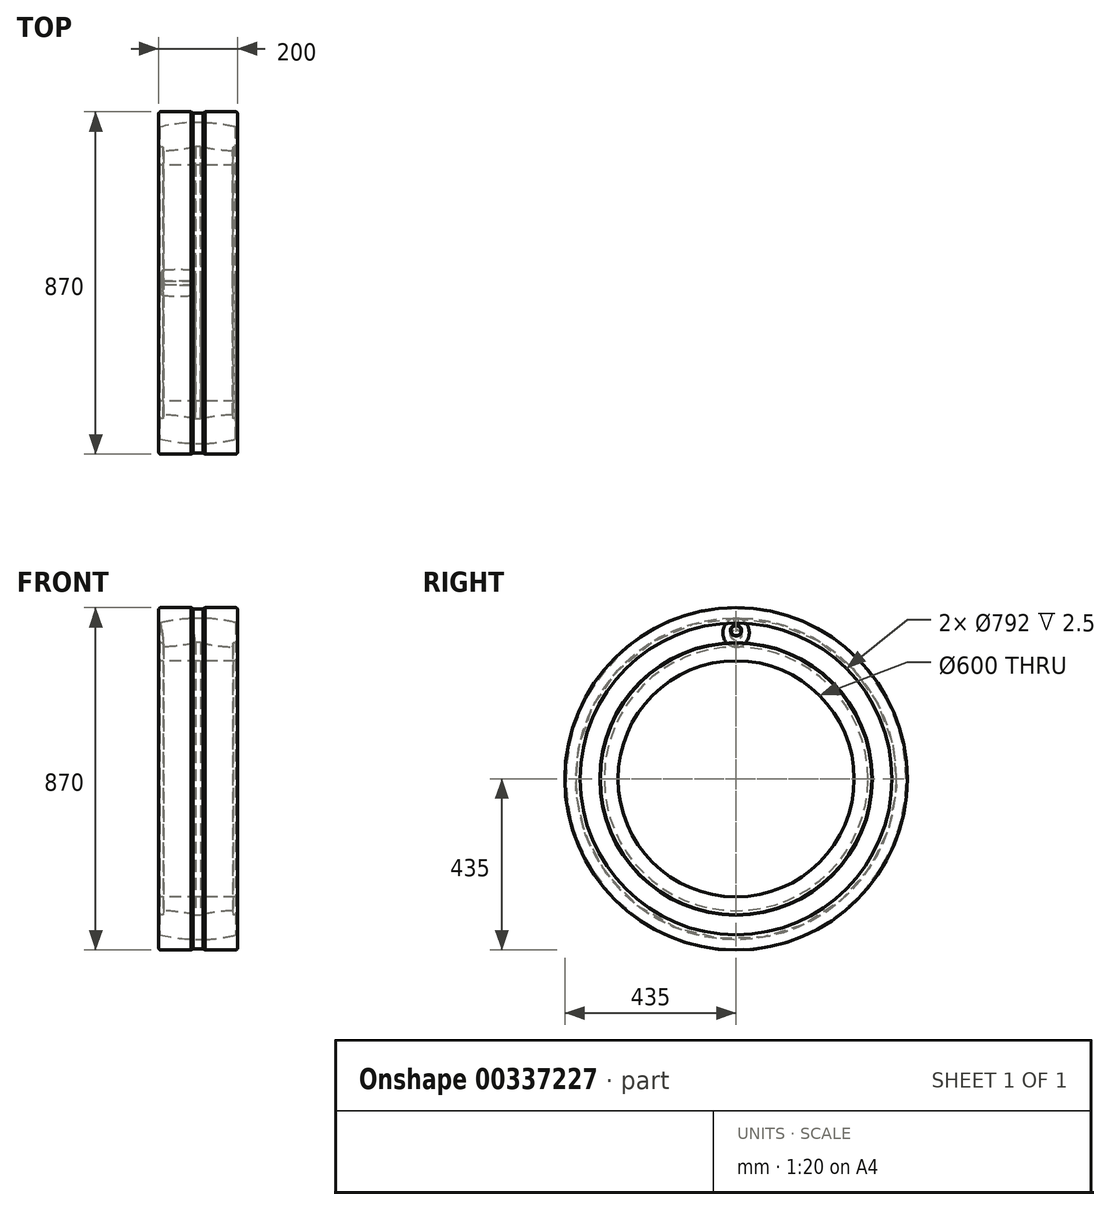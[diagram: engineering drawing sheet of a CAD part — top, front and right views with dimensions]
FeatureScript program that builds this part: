
annotation { "Feature Type Name" : "Feature", "Feature Type Description" : "" }
export const myFeature = defineFeature(function(context is Context, id is Id, definition is map)
    precondition{}
    {
        {
            var Q0;
            Q0=qCreatedBy(makeId("Front.planeOp"),FACE);
            var sketch = newSketch(context, id + "F0", { "sketchPlane" : qUnion([Q0])});
            skLineSegment(sketch, "E0", {"start": v(-95, 300) * mm, "end": v(95, 300) * mm});
            skLineSegment(sketch, "E1", {"start": v(0, 300) * mm, "end": v(0, 0) * mm, "construction": true});
            skLineSegment(sketch, "E2", {"start": v(-100, 305) * mm, "end": v(-100, 342) * mm});
            skLineSegment(sketch, "E3", {"start": v(100, 305) * mm, "end": v(100, 342) * mm});
            skArc(sketch, "E4", {"start": v(-100, 305) * mm, "mid": v(-98.54, 301.46) * mm, "end": v(-95, 300) * mm});
            skArc(sketch, "E5", {"start": v(95, 300) * mm, "mid": v(98.54, 301.46) * mm, "end": v(100, 305) * mm});
            skLineSegment(sketch, "E6", {"start": v(-97, 345) * mm, "end": v(-89, 345) * mm});
            skLineSegment(sketch, "E7", {"start": v(-89, 345) * mm, "end": v(-87.6, 335) * mm});
            skLineSegment(sketch, "E8", {"start": v(97, 345) * mm, "end": v(89, 345) * mm});
            skLineSegment(sketch, "E9", {"start": v(89, 345) * mm, "end": v(87.6, 335) * mm});
            skPoint(sketch, "E10", {"position": v(0, 1213.53) * mm});
            skPoint(sketch, "E11.visualSharp", {"position": v(-100, 345) * mm});
            skArc(sketch, "E11.filletArc", {"start": v(-97, 345) * mm, "mid": v(-99.12, 344.12) * mm, "end": v(-100, 342) * mm});
            skPoint(sketch, "E12.visualSharp", {"position": v(100, 345) * mm});
            skArc(sketch, "E12.filletArc", {"start": v(100, 342) * mm, "mid": v(99.12, 344.12) * mm, "end": v(97, 345) * mm});
            skArc(sketch, "E13", {"start": v(97.5, 396) * mm, "mid": v(0, 407.83) * mm, "end": v(-97.5, 396) * mm});
            skLineSegment(sketch, "E14", {"start": v(-97.5, 396) * mm, "end": v(-100, 396) * mm});
            skLineSegment(sketch, "E15", {"start": v(-100, 396) * mm, "end": v(-100, 430) * mm});
            skLineSegment(sketch, "E16", {"start": v(97.5, 396) * mm, "end": v(100, 396) * mm});
            skLineSegment(sketch, "E17", {"start": v(100, 396) * mm, "end": v(100, 430) * mm});
            skLineSegment(sketch, "E18", {"start": v(95, 435) * mm, "end": v(17.5, 435) * mm});
            skPoint(sketch, "E19.visualSharp", {"position": v(-100, 435) * mm});
            skArc(sketch, "E19.filletArc", {"start": v(-95, 435) * mm, "mid": v(-98.54, 433.54) * mm, "end": v(-100, 430) * mm});
            skPoint(sketch, "E20.visualSharp", {"position": v(100, 435) * mm});
            skArc(sketch, "E20.filletArc", {"start": v(100, 430) * mm, "mid": v(98.54, 433.54) * mm, "end": v(95, 435) * mm});
            skLineSegment(sketch, "E21", {"start": v(-149.52, 0) * mm, "end": v(149.52, 0) * mm, "construction": true});
            skLineSegment(sketch, "E22", {"start": v(-95.52, 395.97) * mm, "end": v(-93.24, 379.61) * mm});
            skLineSegment(sketch, "E23", {"start": v(-93.24, 379.61) * mm, "end": v(-92.11, 378.76) * mm});
            skLineSegment(sketch, "E24", {"start": v(-92.11, 378.76) * mm, "end": v(-90.32, 365.88) * mm});
            skLineSegment(sketch, "E25", {"start": v(-88.53, 353) * mm, "end": v(-89.38, 351.88) * mm, "construction": true});
            skLineSegment(sketch, "E26", {"start": v(-89.38, 351.88) * mm, "end": v(-87.1, 335.53) * mm, "construction": true});
            skArc(sketch, "E27", {"start": v(-17.35, 408.1) * mm, "mid": v(-56.32, 404.44) * mm, "end": v(-94.76, 397.08) * mm});
            skArc(sketch, "E28", {"start": v(-86.07, 334.66) * mm, "mid": v(-47.08, 338.08) * mm, "end": v(-8.6, 345.22) * mm, "construction": true});
            skLineSegment(sketch, "E29", {"start": v(-16.32, 407.23) * mm, "end": v(-14.04, 390.88) * mm});
            skLineSegment(sketch, "E30", {"start": v(-14.04, 390.88) * mm, "end": v(-14.56, 389.56) * mm});
            skLineSegment(sketch, "E31", {"start": v(-14.56, 389.56) * mm, "end": v(-12.76, 376.68) * mm});
            skLineSegment(sketch, "E32", {"start": v(-10.97, 363.8) * mm, "end": v(-10.11, 362.69) * mm, "construction": true});
            skLineSegment(sketch, "E33", {"start": v(-10.11, 362.69) * mm, "end": v(-7.84, 346.33) * mm, "construction": true});
            skPoint(sketch, "E34.visualSharp", {"position": v(-95.64, 396.86) * mm});
            skLineSegment(sketch, "E35", {"start": v(-90.32, 365.88) * mm, "end": v(-12.76, 376.68) * mm});
            skLineSegment(sketch, "E36", {"start": v(-12.76, 376.68) * mm, "end": v(-10.97, 363.8) * mm, "construction": true});
            skLineSegment(sketch, "E37", {"start": v(-90.32, 365.88) * mm, "end": v(-88.53, 353) * mm, "construction": true});
            skArc(sketch, "E38.filletArc", {"start": v(-94.76, 397.08) * mm, "mid": v(-95.36, 396.67) * mm, "end": v(-95.52, 395.97) * mm});
            skPoint(sketch, "E39.visualSharp", {"position": v(-16.44, 408.13) * mm});
            skArc(sketch, "E39.filletArc", {"start": v(-16.32, 407.23) * mm, "mid": v(-16.67, 407.86) * mm, "end": v(-17.35, 408.1) * mm});
            skPoint(sketch, "E40.visualSharp", {"position": v(-86.98, 334.63) * mm});
            skArc(sketch, "E40.filletArc", {"start": v(-87.1, 335.53) * mm, "mid": v(-86.75, 334.9) * mm, "end": v(-86.07, 334.66) * mm, "construction": true});
            skPoint(sketch, "E41.visualSharp", {"position": v(-7.7, 345.43) * mm});
            skArc(sketch, "E41.filletArc", {"start": v(-8.6, 345.22) * mm, "mid": v(-8, 345.63) * mm, "end": v(-7.84, 346.33) * mm, "construction": true});
            skCircle(sketch, "E42", {"center": v(0, 0) * mm, "radius": 25 * mm, "construction": true});
            skLineSegment(sketch, "E43", {"start": v(-56.32, 404.44) * mm, "end": v(-47.08, 338.08) * mm, "construction": true});
            skLineSegment(sketch, "E44", {"start": v(-47.08, 338.08) * mm, "end": v(0, 0) * mm, "construction": true});
            skArc(sketch, "E45", {"start": v(-87.6, 335) * mm, "mid": v(-46.52, 338.56) * mm, "end": v(-6, 346.24) * mm});
            skLineSegment(sketch, "E46", {"start": v(-6, 346.24) * mm, "end": v(6, 346.24) * mm});
            skPoint(sketch, "E47", {"position": v(0, 346.24) * mm});
            skArc(sketch, "E48", {"start": v(6, 346.24) * mm, "mid": v(46.52, 338.56) * mm, "end": v(87.6, 335) * mm});
            skLineSegment(sketch, "E49", {"start": v(-17.5, 435) * mm, "end": v(-12.5, 432) * mm});
            skLineSegment(sketch, "E50", {"start": v(-12.5, 432) * mm, "end": v(12.5, 432) * mm});
            skLineSegment(sketch, "E51", {"start": v(12.5, 432) * mm, "end": v(17.5, 435) * mm});
            skLineSegment(sketch, "E52.trimOffspring", {"start": v(-17.5, 435) * mm, "end": v(-95, 435) * mm});
            skLineSegment(sketch, "E53", {"start": v(-17.5, 435) * mm, "end": v(17.5, 435) * mm, "construction": true});
            skPoint(sketch, "E54", {"position": v(0, 432) * mm});
            skLineSegment(sketch, "E55.MirrorCS", {"start": v(14.04, 390.88) * mm, "end": v(14.56, 389.56) * mm});
            skLineSegment(sketch, "E56.MirrorCS", {"start": v(14.56, 389.56) * mm, "end": v(12.76, 376.68) * mm});
            skLineSegment(sketch, "E57.MirrorCS", {"start": v(90.32, 365.88) * mm, "end": v(12.76, 376.68) * mm});
            skLineSegment(sketch, "E58.MirrorCS", {"start": v(12.76, 376.68) * mm, "end": v(10.97, 363.8) * mm, "construction": true});
            skLineSegment(sketch, "E59.MirrorCS", {"start": v(16.32, 407.23) * mm, "end": v(14.04, 390.88) * mm});
            skLineSegment(sketch, "E60.MirrorCS", {"start": v(93.24, 379.61) * mm, "end": v(92.11, 378.76) * mm});
            skLineSegment(sketch, "E61.MirrorCS", {"start": v(95.52, 395.97) * mm, "end": v(93.24, 379.61) * mm});
            skLineSegment(sketch, "E62.MirrorCS", {"start": v(92.11, 378.76) * mm, "end": v(90.32, 365.88) * mm});
            skArc(sketch, "E63.MirrorCS", {"start": v(17.35, 408.1) * mm, "mid": v(56.32, 404.44) * mm, "end": v(94.76, 397.08) * mm});
            skArc(sketch, "E64.MirrorCS", {"start": v(94.76, 397.08) * mm, "mid": v(95.36, 396.67) * mm, "end": v(95.52, 395.97) * mm});
            skArc(sketch, "E65.MirrorCS", {"start": v(16.32, 407.23) * mm, "mid": v(16.67, 407.86) * mm, "end": v(17.35, 408.1) * mm});
            skSolve(sketch);
        }
        {
            var Q0;
            Q0=makeQuery(id+"F0.imprint","IMPRINT",FACE,{"disambiguationData":[TD([[makeQuery(id+"F0.imprint","IMPRINT",EDGE,{"derivedFrom":sQuery(id+"F0.wireOp",EDGE,"E0")}),1.0]])]});
            var Q1;
            Q1=sQuery(id+"F0.wireOp",EDGE,"E21");
            revolve(context, id + "F1", {"entities" : qUnion([Q0]), "axis" : qUnion([Q1]), "revolveType" : RevolveType.FULL});
        }
        {
            var Q0;
            Q0=makeQuery(id+"F0.imprint","IMPRINT",FACE,{"disambiguationData":[TD([[makeQuery(id+"F0.imprint","IMPRINT",EDGE,{"derivedFrom":sQuery(id+"F0.wireOp",EDGE,"E22")}),1.0]])]});
            var Q1;
            {var subQ5=sQuery(id+"F0.wireOp",EDGE,"E27");Q1=makeQuery(id+"F0.imprint","IMPRINT",FACE,{"disambiguationData":[TD([[makeQuery(id+"F0.imprint","IMPRINT",EDGE,{"derivedFrom":subQ5}),1.0]])]});}
            var Q2;
            Q2=sQuery(id+"F0.wireOp",EDGE,"E35");
            revolve(context, id + "F2", {"operationType" : NewBodyOperationType.ADD, "entities" : qUnion([Q0, Q1]), "axis" : qUnion([Q2]), "revolveType" : RevolveType.FULL});
        }
        {
            var Q0;
            {var subQ7=sQuery(id+"F0.wireOp",EDGE,"E14");Q0=makeQuery(id+"F0.imprint","IMPRINT",FACE,{"disambiguationData":[TD([[makeQuery(id+"F0.imprint","IMPRINT",EDGE,{"derivedFrom":subQ7}),-1.0]])]});}
            var Q1;
            {var subQ5=sQuery(id+"F0.wireOp",EDGE,"E63.MirrorCS");Q1=makeQuery(id+"F0.imprint","IMPRINT",FACE,{"disambiguationData":[TD([[makeQuery(id+"F0.imprint","IMPRINT",EDGE,{"derivedFrom":subQ5}),-1.0]])]});}
            var Q2;
            {var subQ5=sQuery(id+"F0.wireOp",EDGE,"E27");Q2=makeQuery(id+"F0.imprint","IMPRINT",FACE,{"disambiguationData":[TD([[makeQuery(id+"F0.imprint","IMPRINT",EDGE,{"derivedFrom":subQ5}),1.0]])]});}
            var Q3;
            Q3=sQuery(id+"F0.wireOp",EDGE,"E21");
            revolve(context, id + "F3", {"operationType" : NewBodyOperationType.ADD, "entities" : qUnion([Q0, Q1, Q2]), "axis" : qUnion([Q3]), "revolveType" : RevolveType.FULL});
        }
    });
